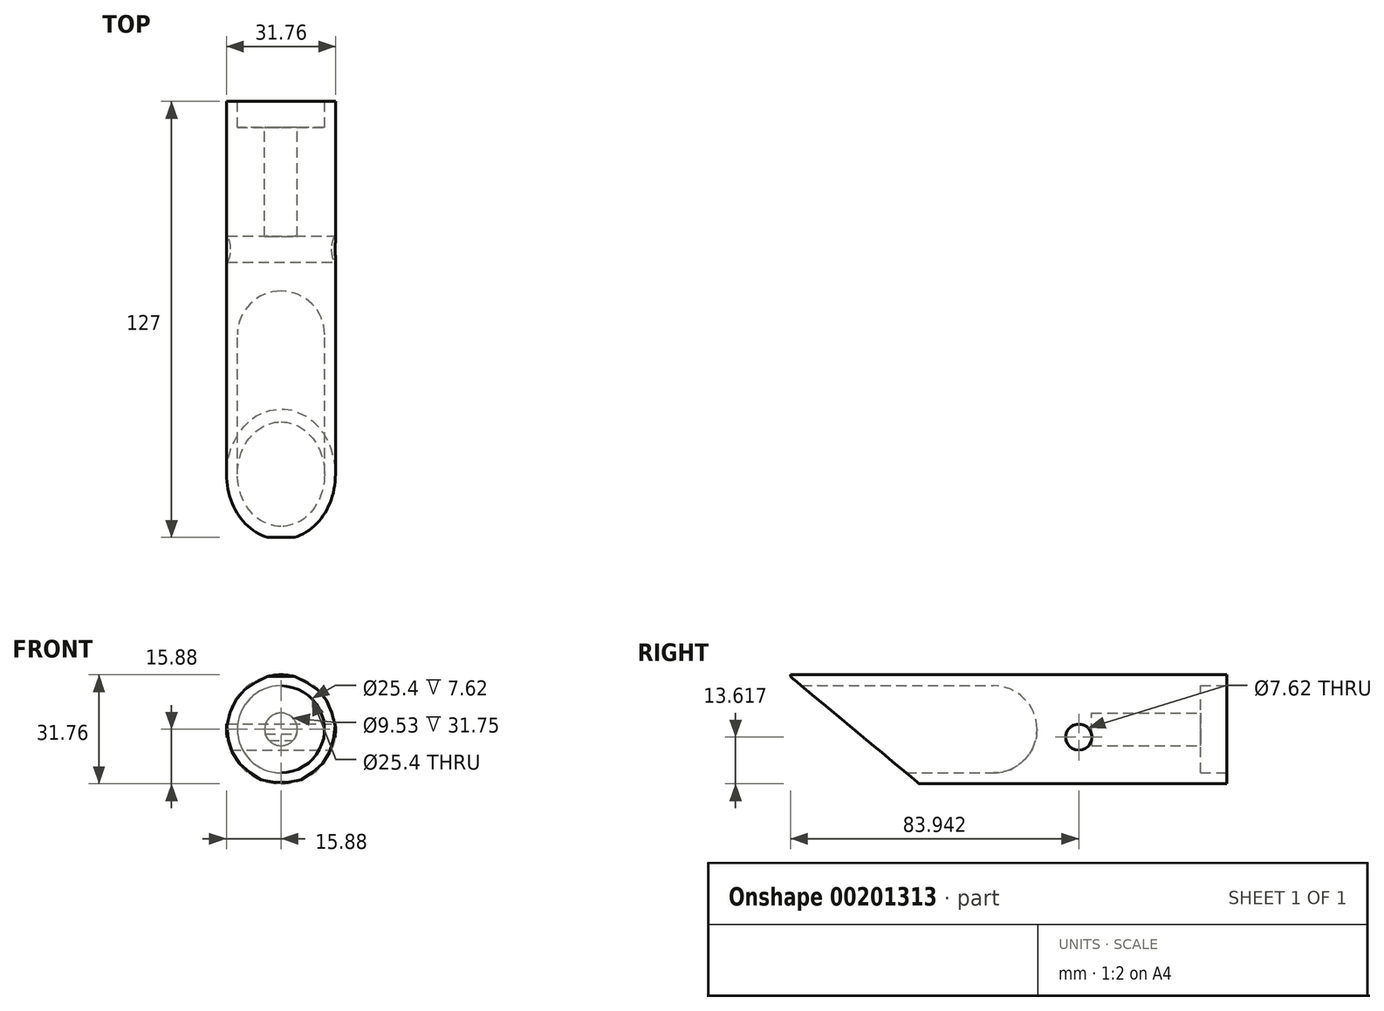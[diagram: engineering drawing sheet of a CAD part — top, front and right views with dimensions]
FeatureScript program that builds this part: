
annotation { "Feature Type Name" : "Feature", "Feature Type Description" : "" }
export const myFeature = defineFeature(function(context is Context, id is Id, definition is map)
    precondition{}
    {
        {
            var Q0;
            Q0=qCreatedBy(makeId("Front.planeOp"),FACE);
            var sketch = newSketch(context, id + "F0", { "sketchPlane" : qUnion([Q0])});
            skCircle(sketch, "E0", {"center": v(0, 0) * mm, "radius": 15.88 * mm});
            skCircle(sketch, "E1", {"center": v(0, 0) * mm, "radius": 12.7 * mm});
            skLineSegment(sketch, "E2", {"start": v(0, 12.7) * mm, "end": v(0, 15.88) * mm});
            skLineSegment(sketch, "E3", {"start": v(0, 15.88) * mm, "end": v(0, 12.7) * mm});
            skSolve(sketch);
        }
        {
            var Q0;
            Q0 = qSketchRegion(id + "F0", true);
            extrude(context, id + "F1", {"entities" : qUnion([Q0]), "depth" : 127 * mm});
        }
        {
            var Q0;
            Q0=qCreatedBy(makeId("Front.planeOp"),FACE);
            cPlane(context, id + "F2", {"entities" : qUnion([Q0]), "cplaneType" : CPlaneType.OFFSET, "offset" : 7.62 * mm, "width" : 152.4 * mm, "height" : 152.4 * mm});
        }
        {
            var Q0;
            Q0=qCreatedBy(id+"F2.planeOp",FACE);
            var sketch = newSketch(context, id + "F3", { "sketchPlane" : qUnion([Q0])});
            skCircle(sketch, "E4", {"center": v(0, 0) * mm, "radius": 12.7 * mm});
            skSolve(sketch);
        }
        {
            var Q0;
            Q0 = qSketchRegion(id + "F3", true);
            extrude(context, id + "F4", {"entities" : qUnion([Q0]), "operationType" : NewBodyOperationType.ADD, "depth" : 40 * mm});
        }
        {
            var Q0;
            Q0=qCreatedBy(id+"F2.planeOp",FACE);
            var sketch = newSketch(context, id + "F5", { "sketchPlane" : qUnion([Q0])});
            skCircle(sketch, "E5", {"center": v(0, 0) * mm, "radius": 4.76 * mm});
            skSolve(sketch);
        }
        {
            var Q0;
            Q0 = qSketchRegion(id + "F5", true);
            extrude(context, id + "F6", {"entities" : qUnion([Q0]), "operationType" : NewBodyOperationType.REMOVE, "depth" : 31.75 * mm});
        }
        {
            var Q0;
            Q0=qCreatedBy(makeId("Right.planeOp"),FACE);
            var sketch = newSketch(context, id + "F7", { "sketchPlane" : qUnion([Q0])});
            skLineSegment(sketch, "E6", {"start": v(-127.26, 15.6) * mm, "end": v(-127.26, -16.16) * mm});
            skLineSegment(sketch, "E7", {"start": v(-127.26, -16.16) * mm, "end": v(-89.16, -16.16) * mm});
            skLineSegment(sketch, "E8", {"start": v(-127.26, 15.6) * mm, "end": v(-89.16, -16.16) * mm});
            skSolve(sketch);
        }
        {
            var Q0;
            Q0 = qSketchRegion(id + "F7", true);
            extrude(context, id + "F8", {"entities" : qUnion([Q0]), "operationType" : NewBodyOperationType.REMOVE, "oppositeDirection" : true, "depth" : 25.4 * mm, "hasSecondDirection" : true, "secondDirectionOppositeDirection" : false, "secondDirectionDepth" : 25.4 * mm});
        }
        {
            var Q0;
            Q0=qCreatedBy(makeId("Right.planeOp"),FACE);
            var sketch = newSketch(context, id + "F9", { "sketchPlane" : qUnion([Q0])});
            skLineSegment(sketch, "E9", {"start": v(0, 0) * mm, "end": v(-43.06, 0) * mm});
            skLineSegment(sketch, "E10", {"start": v(-127.55, 0) * mm, "end": v(-83.1, 0) * mm});
            skCircle(sketch, "E11", {"center": v(-43.06, -2.26) * mm, "radius": 3.81 * mm});
            skSolve(sketch);
        }
        {
            var Q0;
            Q0 = qSketchRegion(id + "F9", true);
            extrude(context, id + "F10", {"entities" : qUnion([Q0]), "operationType" : NewBodyOperationType.REMOVE, "oppositeDirection" : true, "depth" : 25.4 * mm, "hasSecondDirection" : true, "secondDirectionOppositeDirection" : false, "secondDirectionDepth" : 25.4 * mm});
        }
        {
            var Q0;
            Q0=qCreatedBy(makeId("Front.planeOp"),FACE);
            cPlane(context, id + "F11", {"entities" : qUnion([Q0]), "cplaneType" : CPlaneType.OFFSET, "offset" : 47.62 * mm, "width" : 152.4 * mm, "height" : 152.4 * mm});
        }
        {
            var Q0;
            Q0=qCreatedBy(id+"F11.planeOp",FACE);
            var sketch = newSketch(context, id + "F12", { "sketchPlane" : qUnion([Q0])});
            skCircle(sketch, "E12", {"center": v(0, 0) * mm, "radius": 12.7 * mm});
            skSolve(sketch);
        }
        {
            var Q0;
            Q0 = qSketchRegion(id + "F12", true);
            extrude(context, id + "F13", {"entities" : qUnion([Q0]), "operationType" : NewBodyOperationType.ADD, "depth" : 7.62 * mm});
        }
        {
            var Q0;
            Q0=makeQuery(id+"F13.opExtrude","CAP_FACE",FACE,{"disambiguationData":[OSD([sQuery(id+"F12.wireOp",EDGE,"E12")])],"isStart":false});
            fillet(context, id + "F14", {"entities" : qUnion([Q0]), "radius" : 12.7 * mm, "tangentPropagation" : true, "allowEdgeOverflow" : false});
        }
    });
